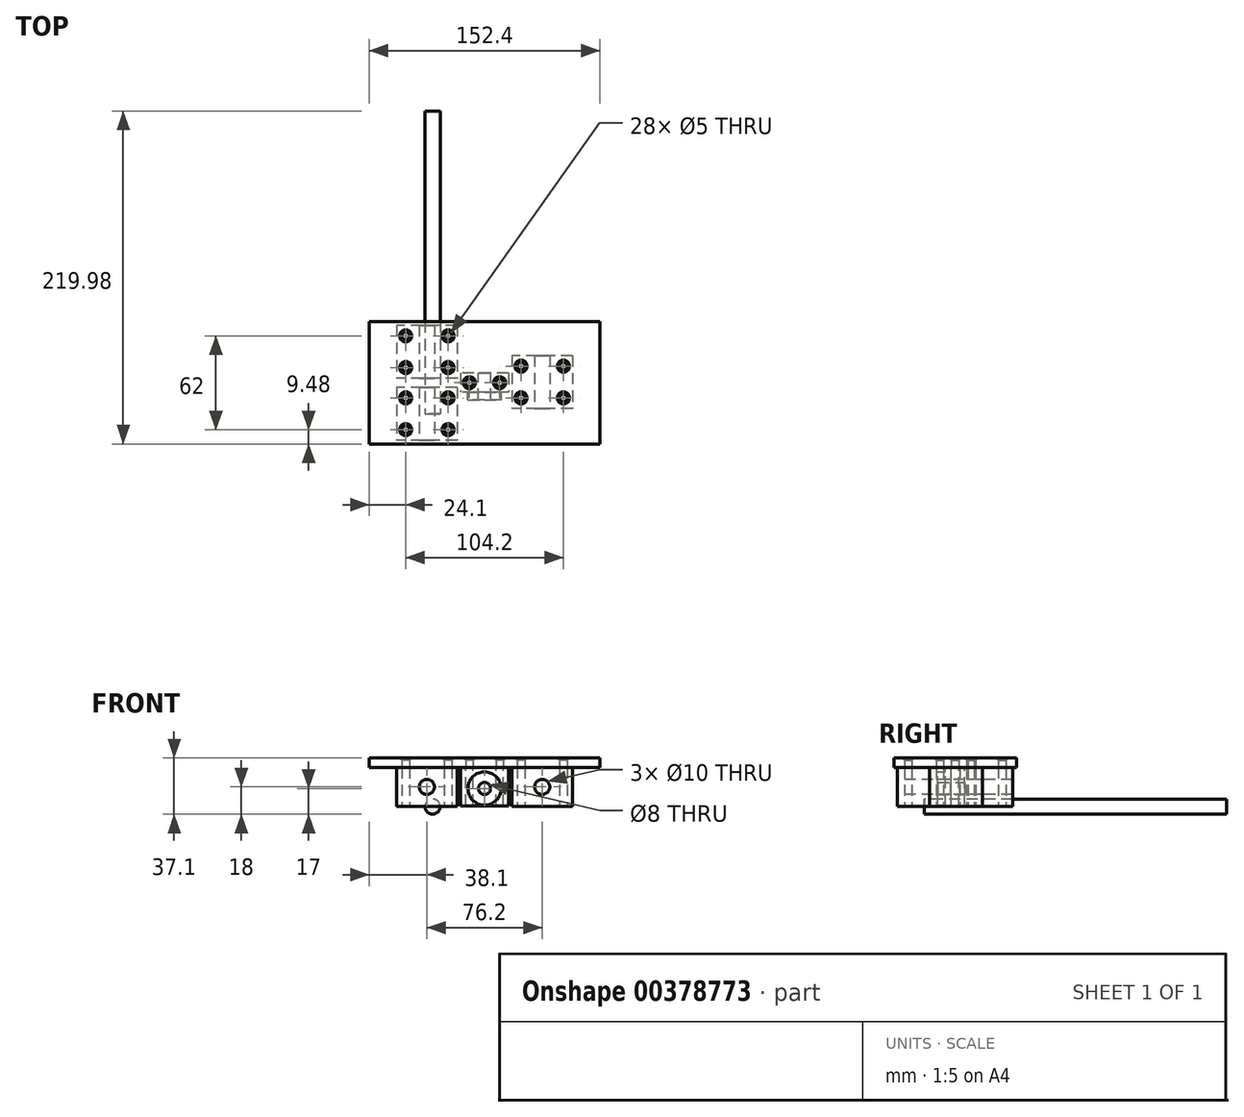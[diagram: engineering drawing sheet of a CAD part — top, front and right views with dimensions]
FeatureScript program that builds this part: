
annotation { "Feature Type Name" : "Feature", "Feature Type Description" : "" }
export const myFeature = defineFeature(function(context is Context, id is Id, definition is map)
    precondition{}
    {
        {
            var Q0;
            Q0=qCreatedBy(makeId("Top.planeOp"),FACE);
            var sketch = newSketch(context, id + "F0", { "sketchPlane" : qUnion([Q0])});
            skLineSegment(sketch, "E0.bottom", {"start": v(20, 17.5) * mm, "end": v(-20, 17.5) * mm});
            skLineSegment(sketch, "E0.top", {"start": v(20, -17.5) * mm, "end": v(-20, -17.5) * mm});
            skLineSegment(sketch, "E0.left", {"start": v(20, 17.5) * mm, "end": v(20, -17.5) * mm});
            skLineSegment(sketch, "E0.right", {"start": v(-20, 17.5) * mm, "end": v(-20, -17.5) * mm});
            skPoint(sketch, "E0.middle", {"position": v(0, 0) * mm});
            skCircle(sketch, "E1", {"center": v(-14, -10.5) * mm, "radius": 2.5 * mm});
            skCircle(sketch, "E2.0.1.0", {"center": v(-14, 10.5) * mm, "radius": 2.5 * mm});
            skCircle(sketch, "E2.1.0.0", {"center": v(14, -10.5) * mm, "radius": 2.5 * mm});
            skCircle(sketch, "E2.1.1.0", {"center": v(14, 10.5) * mm, "radius": 2.5 * mm});
            skLineSegment(sketch, "E2.direction1", {"start": v(-14, -10.5) * mm, "end": v(14, -10.5) * mm, "construction": true});
            skLineSegment(sketch, "E2.direction2", {"start": v(-14, -10.5) * mm, "end": v(-14, 10.5) * mm, "construction": true});
            skSolve(sketch);
        }
        {
            var Q0;
            Q0=makeQuery(id+"F0.imprint","IMPRINT",FACE,{"disambiguationData":[TD([[makeQuery(id+"F0.imprint","IMPRINT",EDGE,{"derivedFrom":sQuery(id+"F0.wireOp",EDGE,"E0.bottom")}),1.0]])]});
            extrude(context, id + "F1", {"entities" : qUnion([Q0]), "depth" : 26 * mm});
        }
        {
            var Q0;
            Q0=makeQuery(id+"F1.opExtrude","SWEPT_FACE",FACE,{"disambiguationData":[OSD([sQuery(id+"F0.wireOp",EDGE,"E0.top")])]});
            var sketch = newSketch(context, id + "F2", { "sketchPlane" : qUnion([Q0])});
            skCircle(sketch, "E3", {"center": v(0, 13) * mm, "radius": 5 * mm});
            skPoint(sketch, "E3.centerSnap0", {"position": v(-20, 13) * mm});
            skSolve(sketch);
        }
        {
            var Q0;
            Q0=makeQuery(id+"F2.imprint","IMPRINT",FACE,{"disambiguationData":[TD([[makeQuery(id+"F2.imprint","IMPRINT",EDGE,{"derivedFrom":sQuery(id+"F2.wireOp",EDGE,"E3")}),1.0]])]});
            extrude(context, id + "F3", {"entities" : qUnion([Q0]), "operationType" : NewBodyOperationType.REMOVE, "endBound" : BoundingType.UP_TO_NEXT, "oppositeDirection" : true, "depth" : 25 * mm});
        }
        {
            var Q0;
            Q0=qCreatedBy(makeId("Front.planeOp"),FACE);
            var sketch = newSketch(context, id + "F4", { "sketchPlane" : qUnion([Q0])});
            skCircle(sketch, "E4", {"center": v(3.8, 0) * mm, "radius": 5 * mm});
            skSolve(sketch);
        }
        {
            var Q0;
            Q0=makeQuery(id+"F4.imprint","IMPRINT",FACE,{"disambiguationData":[TD([[makeQuery(id+"F4.imprint","IMPRINT",EDGE,{"derivedFrom":sQuery(id+"F4.wireOp",EDGE,"E4")}),1.0]])]});
            extrude(context, id + "F5", {"entities" : qUnion([Q0]), "oppositeDirection" : true, "depth" : 200 * mm});
        }
        {
            var Q0;
            Q0=makeQuery(id+"F1.opExtrude","SWEPT_BODY",BODY,{"disambiguationData":[OSD([sQuery(id+"F0.wireOp",EDGE,"E0.bottom"),sQuery(id+"F0.wireOp",EDGE,"E0.top"),sQuery(id+"F0.wireOp",EDGE,"E0.left"),sQuery(id+"F0.wireOp",EDGE,"E0.right"),sQuery(id+"F0.wireOp",EDGE,"E1"),sQuery(id+"F0.wireOp",EDGE,"E2.0.1.0"),sQuery(id+"F0.wireOp",EDGE,"E2.1.0.0"),sQuery(id+"F0.wireOp",EDGE,"E2.1.1.0")])]});
            transform(context, id + "F6", {"entities" : qUnion([Q0]), "transformType" : TransformType.TRANSLATION_3D, "dx" : 0 * mm, "dy" : 41 * mm, "dz" : 0 * mm, "makeCopy" : true});
        }
        {
            var Q0;
            Q0=makeQuery(id+"F1.opExtrude","SWEPT_BODY",BODY,{"disambiguationData":[OSD([sQuery(id+"F0.wireOp",EDGE,"E0.bottom"),sQuery(id+"F0.wireOp",EDGE,"E0.top"),sQuery(id+"F0.wireOp",EDGE,"E0.left"),sQuery(id+"F0.wireOp",EDGE,"E0.right"),sQuery(id+"F0.wireOp",EDGE,"E1"),sQuery(id+"F0.wireOp",EDGE,"E2.0.1.0"),sQuery(id+"F0.wireOp",EDGE,"E2.1.0.0"),sQuery(id+"F0.wireOp",EDGE,"E2.1.1.0")])]});
            transform(context, id + "F7", {"entities" : qUnion([Q0]), "transformType" : TransformType.TRANSLATION_3D, "dx" : 76.2 * mm, "dy" : 21 * mm, "dz" : 0 * mm, "makeCopy" : true});
        }
        {
            var Q0;
            Q0=makeQuery(id+"F1.opExtrude","CAP_FACE",FACE,{"disambiguationData":[OSD([sQuery(id+"F0.wireOp",EDGE,"E0.bottom"),sQuery(id+"F0.wireOp",EDGE,"E0.top"),sQuery(id+"F0.wireOp",EDGE,"E0.left"),sQuery(id+"F0.wireOp",EDGE,"E0.right"),sQuery(id+"F0.wireOp",EDGE,"E1"),sQuery(id+"F0.wireOp",EDGE,"E2.0.1.0"),sQuery(id+"F0.wireOp",EDGE,"E2.1.0.0"),sQuery(id+"F0.wireOp",EDGE,"E2.1.1.0")])],"isStart":false});
            var sketch = newSketch(context, id + "F8", { "sketchPlane" : qUnion([Q0])});
            skLineSegment(sketch, "E5.bottom", {"start": v(-38.1, -19.98) * mm, "end": v(114.3, -19.98) * mm});
            skLineSegment(sketch, "E5.top", {"start": v(-38.1, 60.98) * mm, "end": v(114.3, 60.98) * mm});
            skLineSegment(sketch, "E5.left", {"start": v(-38.1, -19.98) * mm, "end": v(-38.1, 60.98) * mm});
            skLineSegment(sketch, "E5.right", {"start": v(114.3, -19.98) * mm, "end": v(114.3, 60.98) * mm});
            skLineSegment(sketch, "E6", {"start": v(-14, 51.5) * mm, "end": v(-14, -10.5) * mm, "construction": true});
            skLineSegment(sketch, "E7", {"start": v(-14, 51.5) * mm, "end": v(14, 51.5) * mm, "construction": true});
            skLineSegment(sketch, "E8", {"start": v(-14, 30.5) * mm, "end": v(14, 30.5) * mm, "construction": true});
            skLineSegment(sketch, "E9", {"start": v(-14, 10.5) * mm, "end": v(14, 10.5) * mm, "construction": true});
            skLineSegment(sketch, "E10", {"start": v(-14, -10.5) * mm, "end": v(14, -10.5) * mm, "construction": true});
            skLineSegment(sketch, "E11", {"start": v(14, -10.5) * mm, "end": v(14, 51.5) * mm, "construction": true});
            skLineSegment(sketch, "E12", {"start": v(114.3, 20.5) * mm, "end": v(-38.1, 20.5) * mm, "construction": true});
            skCircle(sketch, "E13", {"center": v(-14, 30.5) * mm, "radius": 2.5 * mm});
            skCircle(sketch, "E14", {"center": v(14, 30.5) * mm, "radius": 2.5 * mm});
            skCircle(sketch, "E15", {"center": v(-14, 51.5) * mm, "radius": 2.5 * mm});
            skCircle(sketch, "E16", {"center": v(14, 51.5) * mm, "radius": 2.5 * mm});
            skLineSegment(sketch, "E17", {"start": v(0, 0) * mm, "end": v(0, 70.08) * mm, "construction": true});
            skLineSegment(sketch, "E18", {"start": v(76.2, 68.3) * mm, "end": v(76.2, -33.64) * mm, "construction": true});
            skCircle(sketch, "E19", {"center": v(62.2, 31.5) * mm, "radius": 2.5 * mm});
            skCircle(sketch, "E20", {"center": v(90.2, 31.5) * mm, "radius": 2.5 * mm});
            skCircle(sketch, "E21", {"center": v(90.2, 10.5) * mm, "radius": 2.5 * mm});
            skCircle(sketch, "E22", {"center": v(62.2, 10.5) * mm, "radius": 2.5 * mm});
            skLineSegment(sketch, "E23", {"start": v(38.1, 60.98) * mm, "end": v(38.1, -19.98) * mm, "construction": true});
            skLineSegment(sketch, "E24.bottom", {"start": v(53.98, 26.85) * mm, "end": v(22.23, 26.85) * mm});
            skLineSegment(sketch, "E24.top", {"start": v(53.98, 14.15) * mm, "end": v(22.23, 14.15) * mm});
            skLineSegment(sketch, "E24.left", {"start": v(53.98, 26.85) * mm, "end": v(53.98, 14.15) * mm});
            skLineSegment(sketch, "E24.right", {"start": v(22.23, 26.85) * mm, "end": v(22.23, 14.15) * mm});
            skPoint(sketch, "E24.middle", {"position": v(38.1, 20.5) * mm});
            skLineSegment(sketch, "E25.0", {"start": v(42.1, 26.85) * mm, "end": v(42.1, 14.15) * mm});
            skLineSegment(sketch, "E26.0", {"start": v(34.1, 26.85) * mm, "end": v(34.1, 14.15) * mm, "construction": true});
            skLineSegment(sketch, "E27.0", {"start": v(28.1, 26.85) * mm, "end": v(28.1, 14.15) * mm, "construction": true});
            skLineSegment(sketch, "E28.0", {"start": v(48.1, 26.85) * mm, "end": v(48.1, 14.15) * mm, "construction": true});
            skCircle(sketch, "E29", {"center": v(48.1, 20.5) * mm, "radius": 2.5 * mm});
            skCircle(sketch, "E30", {"center": v(28.1, 20.5) * mm, "radius": 2.5 * mm});
            skSolve(sketch);
        }
        {
            var Q0;
            Q0=makeQuery(id+"F8.imprint","IMPRINT",FACE,{"disambiguationData":[TD([[makeQuery(id+"F8.imprint","IMPRINT",EDGE,{"derivedFrom":sQuery(id+"F8.wireOp",EDGE,"E5.bottom")}),1.0]])]});
            var Q1;
            Q1=makeQuery(id+"F8.imprint","IMPRINT",FACE,{"disambiguationData":[TD([[makeQuery(id+"F8.imprint","IMPRINT",EDGE,{"derivedFrom":makeQuery(id+"F1.opExtrude","CAP_EDGE",EDGE,{"disambiguationData":[OSD([sQuery(id+"F0.wireOp",EDGE,"E0.bottom")])],"isStart":false})}),1.0]])]});
            var Q2;
            {var subQ0=sQuery(id+"F8.wireOp",EDGE,"E24.right");Q2=makeQuery(id+"F8.imprint","IMPRINT",FACE,{"disambiguationData":[TD([[makeQuery(id+"F8.imprint","IMPRINT",EDGE,{"derivedFrom":subQ0}),1.0]])]});}
            var Q3;
            {var subQ1=sQuery(id+"F8.wireOp",EDGE,"E24.left");Q3=makeQuery(id+"F8.imprint","IMPRINT",FACE,{"disambiguationData":[TD([[makeQuery(id+"F8.imprint","IMPRINT",EDGE,{"derivedFrom":subQ1}),-1.0]])]});}
            extrude(context, id + "F9", {"entities" : qUnion([Q0, Q1, Q2, Q3]), "depth" : 6.1 * mm});
        }
        {
            var Q0;
            Q0=makeQuery(id+"F9.opExtrude","CAP_EDGE",EDGE,{"disambiguationData":[OSD([sQuery(id+"F0.wireOp",EDGE,"E2.0.1.0")])],"isStart":false});
            var Q1;
            Q1=makeQuery(id+"F9.opExtrude","CAP_EDGE",EDGE,{"disambiguationData":[OSD([sQuery(id+"F0.wireOp",EDGE,"E1")])],"isStart":false});
            var Q2;
            Q2=makeQuery(id+"F9.opExtrude","CAP_EDGE",EDGE,{"disambiguationData":[OSD([sQuery(id+"F0.wireOp",EDGE,"E2.1.0.0")])],"isStart":false});
            var Q3;
            Q3=makeQuery(id+"F9.opExtrude","CAP_EDGE",EDGE,{"disambiguationData":[OSD([sQuery(id+"F0.wireOp",EDGE,"E2.1.1.0")])],"isStart":false});
            var Q4;
            Q4=makeQuery(id+"F9.opExtrude","CAP_EDGE",EDGE,{"disambiguationData":[OSD([sQuery(id+"F8.wireOp",EDGE,"E13")])],"isStart":false});
            var Q5;
            Q5=makeQuery(id+"F9.opExtrude","CAP_EDGE",EDGE,{"disambiguationData":[OSD([sQuery(id+"F8.wireOp",EDGE,"E15")])],"isStart":false});
            var Q6;
            Q6=makeQuery(id+"F9.opExtrude","CAP_EDGE",EDGE,{"disambiguationData":[OSD([sQuery(id+"F8.wireOp",EDGE,"E16")])],"isStart":false});
            var Q7;
            Q7=makeQuery(id+"F9.opExtrude","CAP_EDGE",EDGE,{"disambiguationData":[OSD([sQuery(id+"F8.wireOp",EDGE,"E14")])],"isStart":false});
            var Q8;
            Q8=makeQuery(id+"F9.opExtrude","CAP_EDGE",EDGE,{"disambiguationData":[OSD([sQuery(id+"F8.wireOp",EDGE,"E19")])],"isStart":false});
            var Q9;
            Q9=makeQuery(id+"F9.opExtrude","CAP_EDGE",EDGE,{"disambiguationData":[OSD([sQuery(id+"F8.wireOp",EDGE,"E22")])],"isStart":false});
            var Q10;
            Q10=makeQuery(id+"F9.opExtrude","CAP_EDGE",EDGE,{"disambiguationData":[OSD([sQuery(id+"F8.wireOp",EDGE,"E20")])],"isStart":false});
            var Q11;
            Q11=makeQuery(id+"F9.opExtrude","CAP_EDGE",EDGE,{"disambiguationData":[OSD([sQuery(id+"F8.wireOp",EDGE,"E21")])],"isStart":false});
            var Q12;
            Q12=makeQuery(id+"F9.opExtrude","CAP_EDGE",EDGE,{"disambiguationData":[OSD([sQuery(id+"F8.wireOp",EDGE,"E30")])],"isStart":false});
            var Q13;
            Q13=makeQuery(id+"F9.opExtrude","CAP_EDGE",EDGE,{"disambiguationData":[OSD([sQuery(id+"F8.wireOp",EDGE,"E29")])],"isStart":false});
            chamfer(context, id + "F10", {"entities" : qUnion([Q0, Q1, Q2, Q3, Q4, Q5, Q6, Q7, Q8, Q9, Q10, Q11, Q12, Q13]), "width" : 1.5 * mm, "tangentPropagation" : true});
        }
        {
            var Q0;
            Q0=makeQuery(id+"F8.imprint","IMPRINT",FACE,{"disambiguationData":[TD([[makeQuery(id+"F8.imprint","IMPRINT",EDGE,{"derivedFrom":sQuery(id+"F8.wireOp",EDGE,"E24.bottom")}),1.0]])]});
            extrude(context, id + "F11", {"entities" : qUnion([Q0]), "oppositeDirection" : true, "depth" : 25.4 * mm});
        }
        {
            var Q0;
            Q0=makeQuery(id+"F11.opExtrude","SWEPT_FACE",FACE,{"disambiguationData":[OSD([sQuery(id+"F8.wireOp",EDGE,"E24.top")])]});
            var sketch = newSketch(context, id + "F12", { "sketchPlane" : qUnion([Q0])});
            skCircle(sketch, "E31", {"center": v(38.1, 12) * mm, "radius": 11 * mm});
            skLineSegment(sketch, "E32", {"start": v(38.1, 26) * mm, "end": v(38.1, -2.22) * mm, "construction": true});
            skPoint(sketch, "E32.endSnap0", {"position": v(38.1, 26) * mm});
            skLineSegment(sketch, "E33", {"start": v(22.21, 12) * mm, "end": v(53.99, 12) * mm, "construction": true});
            skCircle(sketch, "E34", {"center": v(38.1, 12) * mm, "radius": 4 * mm});
            skSolve(sketch);
        }
        {
            var Q0;
            Q0 = qSketchRegion(id + "F12", true);
            extrude(context, id + "F13", {"entities" : qUnion([Q0]), "operationType" : NewBodyOperationType.ADD, "depth" : 5 * mm});
        }
        {
            var Q0;
            Q0=makeQuery(id+"F13.boolean.opBoolean","SPLIT",FACE,{"disambiguationData":[TD([makeQuery(id+"F13.opExtrude","SWEPT_FACE",FACE,{"disambiguationData":[OSD([sQuery(id+"F12.wireOp",EDGE,"E34")])]})])],"derivedFrom":makeQuery(id+"F11.opExtrude","SWEPT_FACE",FACE,{"disambiguationData":[OSD([sQuery(id+"F8.wireOp",EDGE,"E24.top")])]})});
            extrude(context, id + "F14", {"entities" : qUnion([Q0]), "operationType" : NewBodyOperationType.REMOVE, "endBound" : BoundingType.UP_TO_NEXT, "oppositeDirection" : true, "depth" : 25 * mm});
        }
    });
